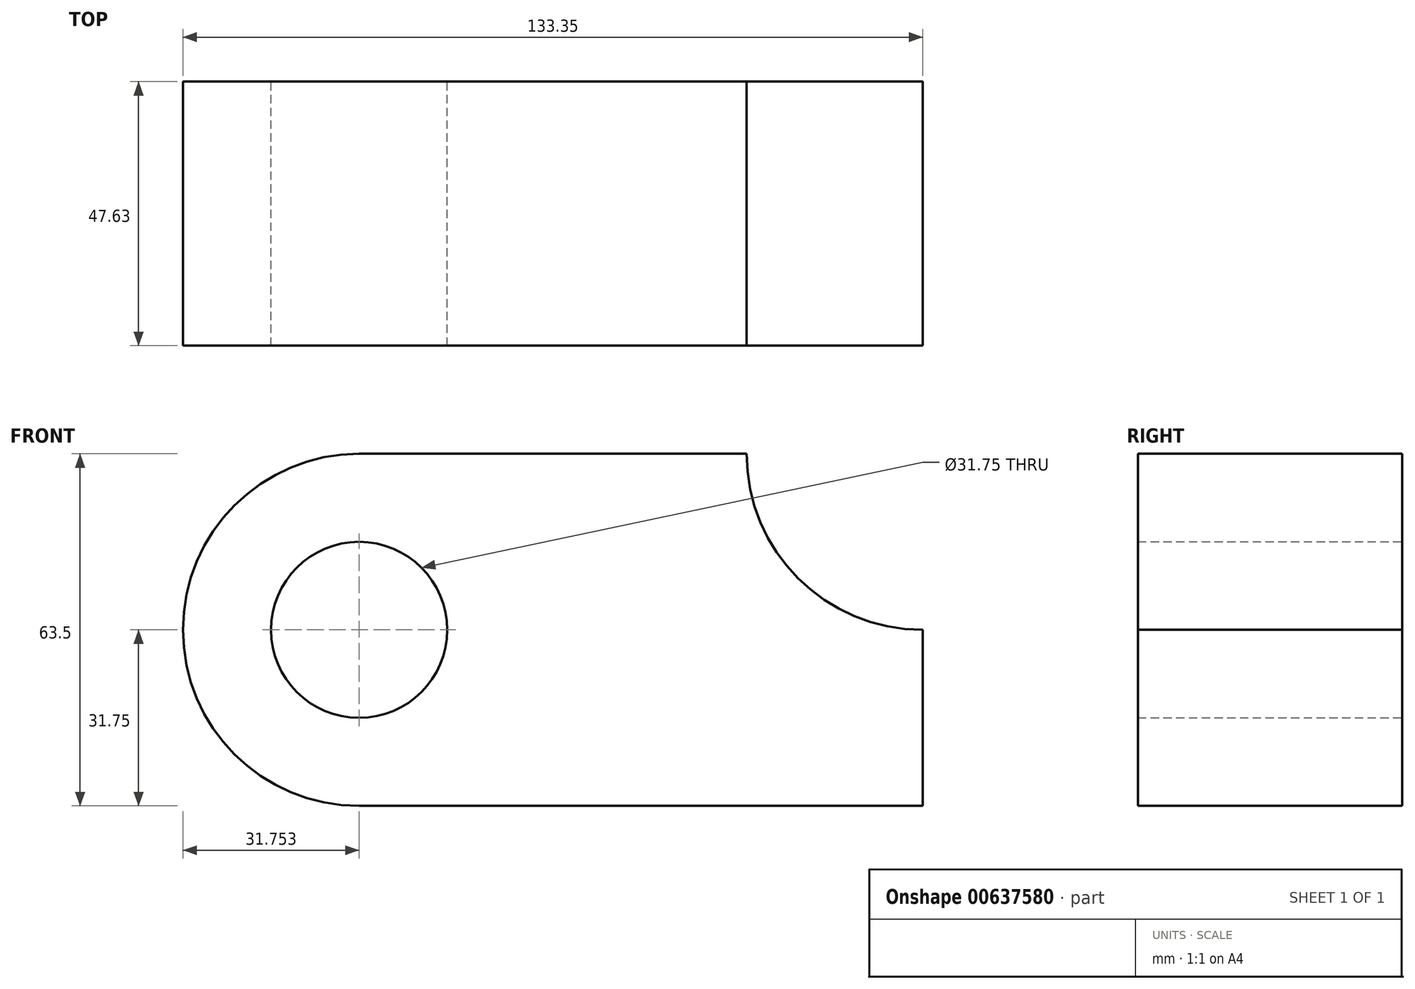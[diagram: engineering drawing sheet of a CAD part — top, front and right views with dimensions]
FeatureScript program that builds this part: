
annotation { "Feature Type Name" : "Feature", "Feature Type Description" : "" }
export const myFeature = defineFeature(function(context is Context, id is Id, definition is map)
    precondition{}
    {
        {
            var Q0;
            Q0=qCreatedBy(makeId("Front.planeOp"),FACE);
            var sketch = newSketch(context, id + "F0", { "sketchPlane" : qUnion([Q0])});
            skLineSegment(sketch, "E0", {"start": v(-65.49, 0) * mm, "end": v(36.11, 0) * mm});
            skLineSegment(sketch, "E1", {"start": v(36.11, 0) * mm, "end": v(36.11, 31.75) * mm});
            skLineSegment(sketch, "E2", {"start": v(4.36, 63.5) * mm, "end": v(-65.49, 63.5) * mm});
            skArc(sketch, "E3", {"start": v(-65.49, 63.5) * mm, "mid": v(-97.24, 31.75) * mm, "end": v(-65.49, 0) * mm});
            skArc(sketch, "E4", {"start": v(4.36, 63.5) * mm, "mid": v(13.66, 41.05) * mm, "end": v(36.11, 31.75) * mm});
            skCircle(sketch, "E5", {"center": v(-65.49, 31.75) * mm, "radius": 15.88 * mm});
            skSolve(sketch);
        }
        {
            var Q0;
            Q0=makeQuery(id+"F0.imprint","IMPRINT",FACE,{"disambiguationData":[TD([[makeQuery(id+"F0.imprint","IMPRINT",EDGE,{"derivedFrom":sQuery(id+"F0.wireOp",EDGE,"E0")}),1.0]])]});
            extrude(context, id + "F1", {"entities" : qUnion([Q0]), "depth" : 47.62 * mm, "offsetDistance" : 25.4 * mm});
        }
    });
